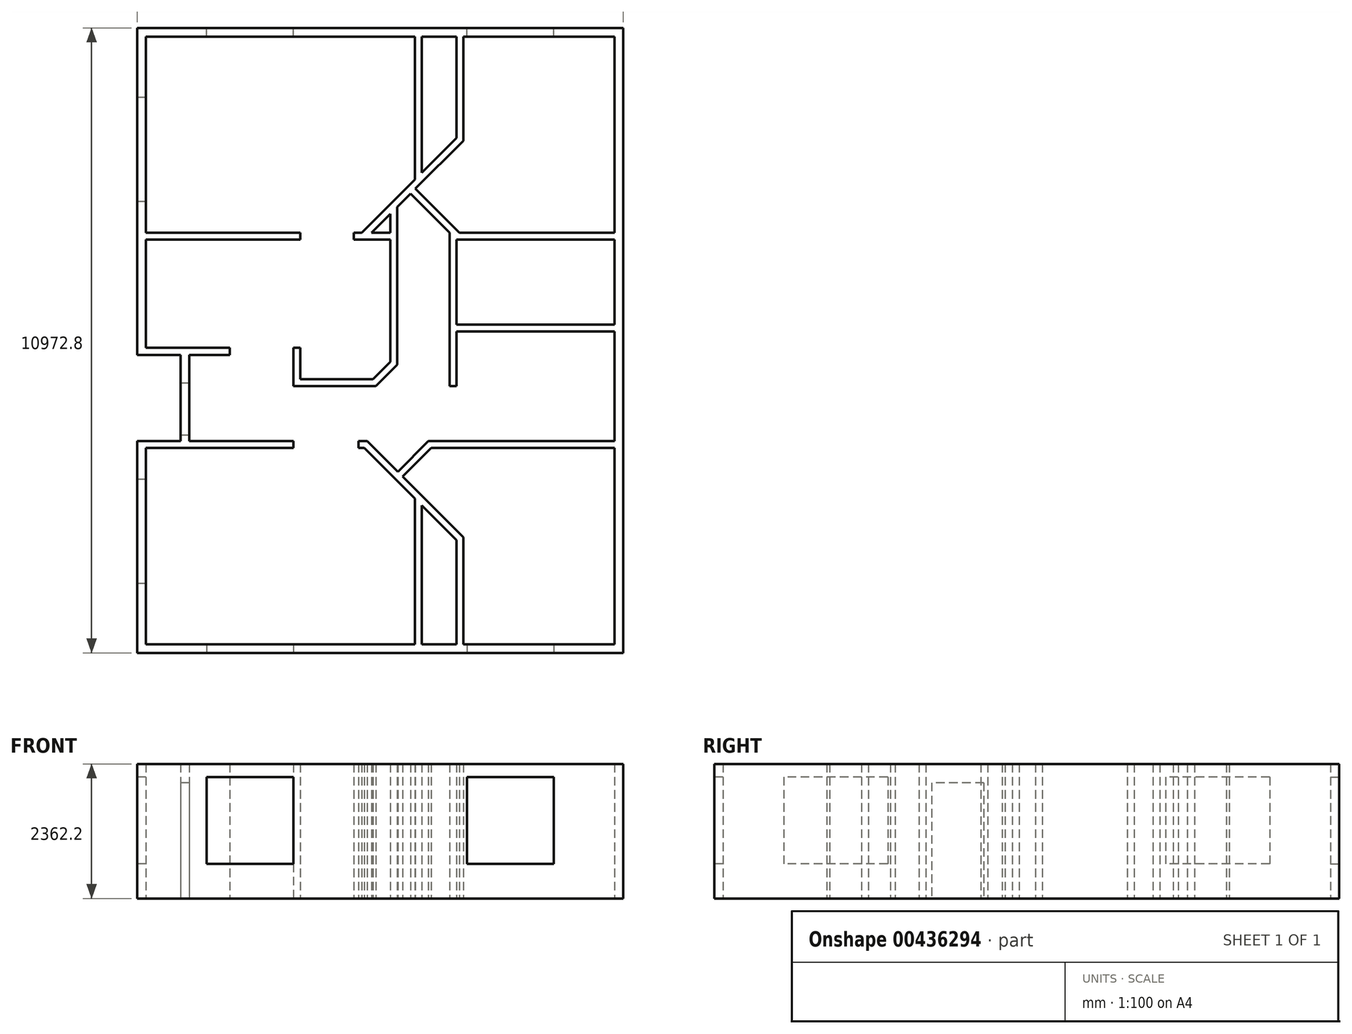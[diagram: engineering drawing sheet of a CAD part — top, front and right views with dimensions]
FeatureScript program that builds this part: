
annotation { "Feature Type Name" : "Feature", "Feature Type Description" : "" }
export const myFeature = defineFeature(function(context is Context, id is Id, definition is map)
    precondition{}
    {
        {
            var Q0;
            Q0=qCreatedBy(makeId("Top.planeOp"),FACE);
            var sketch = newSketch(context, id + "F0", { "sketchPlane" : qUnion([Q0])});
            skLineSegment(sketch, "E0.bottom", {"start": v(-8534.4, 10972.8) * mm, "end": v(0, 10972.8) * mm});
            skLineSegment(sketch, "E0.top", {"start": v(-8534.4, 0) * mm, "end": v(0, 0) * mm});
            skLineSegment(sketch, "E0.left", {"start": v(-8534.4, 10972.8) * mm, "end": v(-8534.4, 5232.5) * mm});
            skLineSegment(sketch, "E0.right", {"start": v(0, 10972.8) * mm, "end": v(0, 0) * mm});
            skLineSegment(sketch, "E1.bottom", {"start": v(-8382, 10820.4) * mm, "end": v(-3657.6, 10820.4) * mm});
            skLineSegment(sketch, "E1.top", {"start": v(-8382, 7254.24) * mm, "end": v(-5669.28, 7254.24) * mm});
            skLineSegment(sketch, "E1.left", {"start": v(-8382, 10820.4) * mm, "end": v(-8382, 7376.16) * mm});
            skLineSegment(sketch, "E2.bottom", {"start": v(-8382, 152.4) * mm, "end": v(-3657.6, 152.4) * mm});
            skLineSegment(sketch, "E2.top", {"start": v(-8382, 3596.64) * mm, "end": v(-5791.2, 3596.64) * mm});
            skLineSegment(sketch, "E2.left", {"start": v(-8382, 152.4) * mm, "end": v(-8382, 3596.64) * mm});
            skLineSegment(sketch, "E3", {"start": v(-8382, 7376.16) * mm, "end": v(-5669.28, 7376.16) * mm});
            skLineSegment(sketch, "E4", {"start": v(-5669.28, 7254.24) * mm, "end": v(-5669.28, 7376.16) * mm});
            skLineSegment(sketch, "E5", {"start": v(-8382, 7254.24) * mm, "end": v(-8382, 5354.42) * mm});
            skLineSegment(sketch, "E6", {"start": v(-8382, 5354.42) * mm, "end": v(-6908.6, 5354.42) * mm});
            skLineSegment(sketch, "E7", {"start": v(-6908.6, 5354.42) * mm, "end": v(-6908.6, 5232.5) * mm});
            skLineSegment(sketch, "E8", {"start": v(-6908.6, 5232.5) * mm, "end": v(-7620, 5232.5) * mm});
            skLineSegment(sketch, "E9", {"start": v(-7772.4, 5232.5) * mm, "end": v(-7772.4, 3718.56) * mm});
            skLineSegment(sketch, "E10", {"start": v(-7620, 5232.5) * mm, "end": v(-7620, 3718.56) * mm});
            skLineSegment(sketch, "E11", {"start": v(-7620, 3718.56) * mm, "end": v(-5791.2, 3718.56) * mm});
            skLineSegment(sketch, "E12", {"start": v(-5791.2, 3718.56) * mm, "end": v(-5791.2, 3596.64) * mm});
            skLineSegment(sketch, "E13", {"start": v(-8534.4, 7315.2) * mm, "end": v(395.45, 7315.2) * mm, "construction": true});
            skLineSegment(sketch, "E14", {"start": v(-9054.96, 3657.6) * mm, "end": v(470.63, 3657.6) * mm, "construction": true});
            skLineSegment(sketch, "E15", {"start": v(-7772.4, 5232.5) * mm, "end": v(-8534.4, 5232.5) * mm});
            skLineSegment(sketch, "E16", {"start": v(-7772.4, 3718.56) * mm, "end": v(-8534.4, 3718.56) * mm});
            skLineSegment(sketch, "E17.trimOffspring", {"start": v(-8534.4, 3718.56) * mm, "end": v(-8534.4, 0) * mm});
            skLineSegment(sketch, "E18", {"start": v(-3657.6, 152.4) * mm, "end": v(-3657.6, 2707.94) * mm});
            skLineSegment(sketch, "E19", {"start": v(-3657.6, 2707.94) * mm, "end": v(-4546.3, 3596.64) * mm});
            skLineSegment(sketch, "E20", {"start": v(-4546.3, 3596.64) * mm, "end": v(-4648.2, 3596.64) * mm});
            skLineSegment(sketch, "E21", {"start": v(-4648.2, 3596.64) * mm, "end": v(-4648.2, 3718.56) * mm});
            skLineSegment(sketch, "E22", {"start": v(-4648.2, 3718.56) * mm, "end": v(-4495.8, 3718.56) * mm});
            skLineSegment(sketch, "E23", {"start": v(-4495.8, 3718.56) * mm, "end": v(-3956.98, 3179.74) * mm});
            skLineSegment(sketch, "E24", {"start": v(-3956.98, 3179.74) * mm, "end": v(-3418.17, 3718.56) * mm});
            skLineSegment(sketch, "E25", {"start": v(-3418.17, 3718.56) * mm, "end": v(0, 3718.56) * mm});
            skLineSegment(sketch, "E26", {"start": v(-3870.77, 3093.53) * mm, "end": v(-3367.67, 3596.64) * mm});
            skLineSegment(sketch, "E27", {"start": v(-3367.67, 3596.64) * mm, "end": v(-152.4, 3596.64) * mm});
            skLineSegment(sketch, "E28", {"start": v(-152.4, 3596.64) * mm, "end": v(-152.4, 152.4) * mm});
            skLineSegment(sketch, "E29", {"start": v(-152.4, 152.4) * mm, "end": v(-2804.16, 152.4) * mm});
            skLineSegment(sketch, "E30", {"start": v(-3535.68, 152.4) * mm, "end": v(-3535.68, 2586.02) * mm});
            skLineSegment(sketch, "E31", {"start": v(-2926.08, 152.4) * mm, "end": v(-2926.08, 1976.42) * mm});
            skLineSegment(sketch, "E32", {"start": v(-3535.68, 2586.02) * mm, "end": v(-2926.08, 1976.42) * mm});
            skLineSegment(sketch, "E33", {"start": v(-2804.16, 152.4) * mm, "end": v(-2804.16, 2026.92) * mm});
            skLineSegment(sketch, "E34", {"start": v(-2804.16, 2026.92) * mm, "end": v(-3870.77, 3093.53) * mm});
            skLineSegment(sketch, "E35.trimOffspring", {"start": v(-2926.08, 152.4) * mm, "end": v(-3535.68, 152.4) * mm});
            skLineSegment(sketch, "E36", {"start": v(-152.4, 3718.56) * mm, "end": v(-152.4, 5641.54) * mm});
            skLineSegment(sketch, "E37", {"start": v(-152.4, 5641.54) * mm, "end": v(-2926.08, 5641.54) * mm});
            skLineSegment(sketch, "E38", {"start": v(-3048, 5641.54) * mm, "end": v(-3048, 7376.16) * mm});
            skLineSegment(sketch, "E39", {"start": v(-2875.58, 7376.16) * mm, "end": v(-152.4, 7376.16) * mm});
            skLineSegment(sketch, "E40", {"start": v(-152.4, 5763.46) * mm, "end": v(-2926.08, 5763.46) * mm});
            skLineSegment(sketch, "E41", {"start": v(-2926.08, 5763.46) * mm, "end": v(-2926.08, 7254.24) * mm});
            skLineSegment(sketch, "E42", {"start": v(-2926.08, 7254.24) * mm, "end": v(-152.4, 7254.24) * mm});
            skLineSegment(sketch, "E43", {"start": v(-3657.6, 10820.4) * mm, "end": v(-3657.6, 8310.58) * mm});
            skLineSegment(sketch, "E44", {"start": v(-4592.02, 7376.16) * mm, "end": v(-4729.58, 7376.16) * mm});
            skLineSegment(sketch, "E45", {"start": v(-4729.58, 7376.16) * mm, "end": v(-4729.58, 7254.24) * mm});
            skLineSegment(sketch, "E46", {"start": v(-4729.58, 7254.24) * mm, "end": v(-4648.3, 7254.24) * mm});
            skLineSegment(sketch, "E47", {"start": v(-3535.68, 8432.5) * mm, "end": v(-3535.68, 10820.4) * mm});
            skLineSegment(sketch, "E48", {"start": v(-3535.68, 10820.4) * mm, "end": v(-2926.08, 10820.4) * mm});
            skLineSegment(sketch, "E49", {"start": v(-152.4, 10820.4) * mm, "end": v(-152.4, 7376.16) * mm});
            skLineSegment(sketch, "E50", {"start": v(-2804.16, 8991.6) * mm, "end": v(-2804.16, 10820.4) * mm});
            skLineSegment(sketch, "E51", {"start": v(-2926.08, 10820.4) * mm, "end": v(-2926.08, 9042.1) * mm});
            skLineSegment(sketch, "E52", {"start": v(-3967.58, 5059.38) * mm, "end": v(-4343.4, 4683.56) * mm});
            skLineSegment(sketch, "E53", {"start": v(-4343.4, 4683.56) * mm, "end": v(-5791.2, 4683.56) * mm});
            skLineSegment(sketch, "E54", {"start": v(-5791.2, 4683.56) * mm, "end": v(-5791.2, 5354.42) * mm});
            skLineSegment(sketch, "E55", {"start": v(-5791.2, 5354.42) * mm, "end": v(-5669.28, 5354.42) * mm});
            skLineSegment(sketch, "E56", {"start": v(-5669.28, 5354.42) * mm, "end": v(-5669.28, 4805.48) * mm});
            skLineSegment(sketch, "E57", {"start": v(-5669.28, 4805.48) * mm, "end": v(-4393.9, 4805.48) * mm});
            skLineSegment(sketch, "E58", {"start": v(-4393.9, 4805.48) * mm, "end": v(-4089.5, 5109.88) * mm});
            skLineSegment(sketch, "E59", {"start": v(-4089.5, 5109.88) * mm, "end": v(-4089.5, 7254.24) * mm});
            skLineSegment(sketch, "E60", {"start": v(-2804.16, 8991.6) * mm, "end": v(-3647.59, 8148.17) * mm});
            skLineSegment(sketch, "E61", {"start": v(-2926.08, 9042.1) * mm, "end": v(-3535.68, 8432.5) * mm});
            skLineSegment(sketch, "E62", {"start": v(-4648.3, 7254.24) * mm, "end": v(-4089.5, 7254.24) * mm});
            skLineSegment(sketch, "E63", {"start": v(-4419.6, 7376.16) * mm, "end": v(-4089.5, 7376.16) * mm});
            skLineSegment(sketch, "E64", {"start": v(-3048, 7376.16) * mm, "end": v(-3733.8, 8061.96) * mm});
            skLineSegment(sketch, "E65", {"start": v(-3647.59, 8148.17) * mm, "end": v(-2875.58, 7376.16) * mm});
            skLineSegment(sketch, "E66.trimOffspring", {"start": v(-4089.5, 7376.16) * mm, "end": v(-4089.5, 7706.26) * mm});
            skLineSegment(sketch, "E67.trimOffspring", {"start": v(-4089.5, 7706.26) * mm, "end": v(-4419.6, 7376.16) * mm});
            skLineSegment(sketch, "E68.trimOffspring", {"start": v(-3967.58, 7828.18) * mm, "end": v(-3967.58, 5059.38) * mm});
            skLineSegment(sketch, "E69.trimOffspring", {"start": v(-4134.92, 7833.26) * mm, "end": v(-4592.02, 7376.16) * mm});
            skLineSegment(sketch, "E70.trimOffspring", {"start": v(-3733.8, 8061.96) * mm, "end": v(-3967.58, 7828.18) * mm});
            skPoint(sketch, "E71.orphan", {"position": v(-3535.68, 10972.8) * mm});
            skLineSegment(sketch, "E72.trimOffspring", {"start": v(-2804.16, 10820.4) * mm, "end": v(-152.4, 10820.4) * mm});
            skLineSegment(sketch, "E73.trimOffspring", {"start": v(-3657.6, 8310.58) * mm, "end": v(-4134.92, 7833.26) * mm});
            skLineSegment(sketch, "E74", {"start": v(-3228.8, 5702.5) * mm, "end": v(77.15, 5702.5) * mm, "construction": true});
            skLineSegment(sketch, "E75", {"start": v(-3048, 5641.54) * mm, "end": v(-3048, 4683.56) * mm});
            skLineSegment(sketch, "E76", {"start": v(-3048, 4683.56) * mm, "end": v(-2926.08, 4683.56) * mm});
            skLineSegment(sketch, "E77", {"start": v(-2926.08, 4683.56) * mm, "end": v(-2926.08, 5641.54) * mm});
            skPoint(sketch, "E78.orphan", {"position": v(0, 7254.24) * mm});
            skPoint(sketch, "E79.orphan", {"position": v(0, 7376.16) * mm});
            skLineSegment(sketch, "E80.trimOffspring", {"start": v(-152.4, 7254.24) * mm, "end": v(-152.4, 5763.46) * mm});
            skSolve(sketch);
        }
        {
            var Q0;
            {var subQ6=sQuery(id+"F0.wireOp",EDGE,"E0.bottom");Q0=makeQuery(id+"F0.imprint","IMPRINT",FACE,{"disambiguationData":[TD([[makeQuery(id+"F0.imprint","IMPRINT",EDGE,{"derivedFrom":subQ6}),-1.0]])]});}
            extrude(context, id + "F1", {"entities" : qUnion([Q0]), "depth" : 2362.2 * mm});
        }
        {
            var Q0;
            Q0=makeQuery(id+"F1.opExtrude","SWEPT_FACE",FACE,{"disambiguationData":[OSD([sQuery(id+"F0.wireOp",EDGE,"E0.top")])]});
            var sketch = newSketch(context, id + "F2", { "sketchPlane" : qUnion([Q0])});
            skLineSegment(sketch, "E81.bottom", {"start": v(-7315.2, 2133.6) * mm, "end": v(-5791.2, 2133.6) * mm});
            skLineSegment(sketch, "E81.top", {"start": v(-7315.2, 609.6) * mm, "end": v(-5791.2, 609.6) * mm});
            skLineSegment(sketch, "E81.left", {"start": v(-7315.2, 2133.6) * mm, "end": v(-7315.2, 609.6) * mm});
            skLineSegment(sketch, "E81.right", {"start": v(-5791.2, 2133.6) * mm, "end": v(-5791.2, 609.6) * mm});
            skLineSegment(sketch, "E82.bottom", {"start": v(-2743.2, 2133.6) * mm, "end": v(-1219.2, 2133.6) * mm});
            skLineSegment(sketch, "E82.top", {"start": v(-2743.2, 609.6) * mm, "end": v(-1219.2, 609.6) * mm});
            skLineSegment(sketch, "E82.left", {"start": v(-2743.2, 2133.6) * mm, "end": v(-2743.2, 609.6) * mm});
            skLineSegment(sketch, "E82.right", {"start": v(-1219.2, 2133.6) * mm, "end": v(-1219.2, 609.6) * mm});
            skSolve(sketch);
        }
        {
            var Q0;
            Q0=makeQuery(id+"F2.imprint","IMPRINT",FACE,{"disambiguationData":[TD([[makeQuery(id+"F2.imprint","IMPRINT",EDGE,{"derivedFrom":sQuery(id+"F2.wireOp",EDGE,"E81.bottom")}),-1.0]])]});
            var Q1;
            Q1=makeQuery(id+"F2.imprint","IMPRINT",FACE,{"disambiguationData":[TD([[makeQuery(id+"F2.imprint","IMPRINT",EDGE,{"derivedFrom":sQuery(id+"F2.wireOp",EDGE,"E82.bottom")}),-1.0]])]});
            extrude(context, id + "F3", {"entities" : qUnion([Q0, Q1]), "operationType" : NewBodyOperationType.REMOVE, "oppositeDirection" : true, "depth" : 152.4 * mm});
        }
        {
            var Q0;
            Q0=makeQuery(id+"F1.opExtrude","SWEPT_FACE",FACE,{"disambiguationData":[OSD([sQuery(id+"F0.wireOp",EDGE,"E0.left")])]});
            var sketch = newSketch(context, id + "F4", { "sketchPlane" : qUnion([Q0])});
            skLineSegment(sketch, "E83.bottom", {"start": v(-9753.6, 2133.6) * mm, "end": v(-7924.8, 2133.6) * mm});
            skLineSegment(sketch, "E83.top", {"start": v(-9753.6, 609.6) * mm, "end": v(-7924.8, 609.6) * mm});
            skLineSegment(sketch, "E83.left", {"start": v(-9753.6, 2133.6) * mm, "end": v(-9753.6, 609.6) * mm});
            skLineSegment(sketch, "E83.right", {"start": v(-7924.8, 2133.6) * mm, "end": v(-7924.8, 609.6) * mm});
            skLineSegment(sketch, "E84.bottom", {"start": v(-3048, 2133.6) * mm, "end": v(-1219.2, 2133.6) * mm});
            skLineSegment(sketch, "E84.top", {"start": v(-3048, 609.6) * mm, "end": v(-1219.2, 609.6) * mm});
            skLineSegment(sketch, "E84.left", {"start": v(-3048, 2133.6) * mm, "end": v(-3048, 609.6) * mm});
            skLineSegment(sketch, "E84.right", {"start": v(-1219.2, 2133.6) * mm, "end": v(-1219.2, 609.6) * mm});
            skLineSegment(sketch, "E85.bottom", {"start": v(-4734.46, 2031.8) * mm, "end": v(-3820.06, 2031.8) * mm});
            skLineSegment(sketch, "E85.top", {"start": v(-4734.46, 0) * mm, "end": v(-3820.06, 0) * mm});
            skLineSegment(sketch, "E85.left", {"start": v(-4734.46, 2031.8) * mm, "end": v(-4734.46, 0) * mm});
            skLineSegment(sketch, "E85.right", {"start": v(-3820.06, 2031.8) * mm, "end": v(-3820.06, 0) * mm});
            skSolve(sketch);
        }
        {
            var Q0;
            Q0=makeQuery(id+"F4.imprint","IMPRINT",FACE,{"disambiguationData":[TD([[makeQuery(id+"F4.imprint","IMPRINT",EDGE,{"derivedFrom":sQuery(id+"F4.wireOp",EDGE,"E83.bottom")}),-1.0]])]});
            var Q1;
            Q1=makeQuery(id+"F4.imprint","IMPRINT",FACE,{"disambiguationData":[TD([[makeQuery(id+"F4.imprint","IMPRINT",EDGE,{"derivedFrom":sQuery(id+"F4.wireOp",EDGE,"E84.bottom")}),-1.0]])]});
            extrude(context, id + "F5", {"entities" : qUnion([Q0, Q1]), "operationType" : NewBodyOperationType.REMOVE, "oppositeDirection" : true, "depth" : 152.4 * mm});
        }
        {
            var Q0;
            Q0=makeQuery(id+"F1.opExtrude","SWEPT_FACE",FACE,{"disambiguationData":[OSD([sQuery(id+"F0.wireOp",EDGE,"E9")])]});
            var sketch = newSketch(context, id + "F6", { "sketchPlane" : qUnion([Q0])});
            skLineSegment(sketch, "E86.bottom", {"start": v(-4734.46, 2031.8) * mm, "end": v(-3820.06, 2031.8) * mm});
            skLineSegment(sketch, "E86.top", {"start": v(-4734.46, 0) * mm, "end": v(-3820.06, 0) * mm});
            skLineSegment(sketch, "E86.left", {"start": v(-4734.46, 2031.8) * mm, "end": v(-4734.46, 0) * mm});
            skLineSegment(sketch, "E86.right", {"start": v(-3820.06, 2031.8) * mm, "end": v(-3820.06, 0) * mm});
            skSolve(sketch);
        }
        {
            var Q0;
            Q0=makeQuery(id+"F6.imprint","IMPRINT",FACE,{"disambiguationData":[TD([[makeQuery(id+"F6.imprint","IMPRINT",EDGE,{"derivedFrom":sQuery(id+"F6.wireOp",EDGE,"E86.bottom")}),-1.0]])]});
            extrude(context, id + "F7", {"entities" : qUnion([Q0]), "operationType" : NewBodyOperationType.REMOVE, "oppositeDirection" : true, "depth" : 152.4 * mm});
        }
        {
            var Q0;
            Q0=makeQuery(id+"F1.opExtrude","SWEPT_FACE",FACE,{"disambiguationData":[OSD([sQuery(id+"F0.wireOp",EDGE,"E0.bottom")])]});
            var sketch = newSketch(context, id + "F8", { "sketchPlane" : qUnion([Q0])});
            skLineSegment(sketch, "E87.bottom", {"start": v(1219.2, 2133.6) * mm, "end": v(2743.2, 2133.6) * mm});
            skLineSegment(sketch, "E87.top", {"start": v(1219.2, 609.6) * mm, "end": v(2743.2, 609.6) * mm});
            skLineSegment(sketch, "E87.left", {"start": v(1219.2, 2133.6) * mm, "end": v(1219.2, 609.6) * mm});
            skLineSegment(sketch, "E87.right", {"start": v(2743.2, 2133.6) * mm, "end": v(2743.2, 609.6) * mm});
            skLineSegment(sketch, "E88.bottom", {"start": v(5791.2, 2133.6) * mm, "end": v(7315.2, 2133.6) * mm});
            skLineSegment(sketch, "E88.top", {"start": v(5791.2, 609.6) * mm, "end": v(7315.2, 609.6) * mm});
            skLineSegment(sketch, "E88.left", {"start": v(5791.2, 2133.6) * mm, "end": v(5791.2, 609.6) * mm});
            skLineSegment(sketch, "E88.right", {"start": v(7315.2, 2133.6) * mm, "end": v(7315.2, 609.6) * mm});
            skSolve(sketch);
        }
        {
            var Q0;
            Q0=makeQuery(id+"F8.imprint","IMPRINT",FACE,{"disambiguationData":[TD([[makeQuery(id+"F8.imprint","IMPRINT",EDGE,{"derivedFrom":sQuery(id+"F8.wireOp",EDGE,"E88.bottom")}),-1.0]])]});
            var Q1;
            Q1=makeQuery(id+"F8.imprint","IMPRINT",FACE,{"disambiguationData":[TD([[makeQuery(id+"F8.imprint","IMPRINT",EDGE,{"derivedFrom":sQuery(id+"F8.wireOp",EDGE,"E87.bottom")}),-1.0]])]});
            extrude(context, id + "F9", {"entities" : qUnion([Q0, Q1]), "operationType" : NewBodyOperationType.REMOVE, "oppositeDirection" : true, "depth" : 152.4 * mm});
        }
    });
